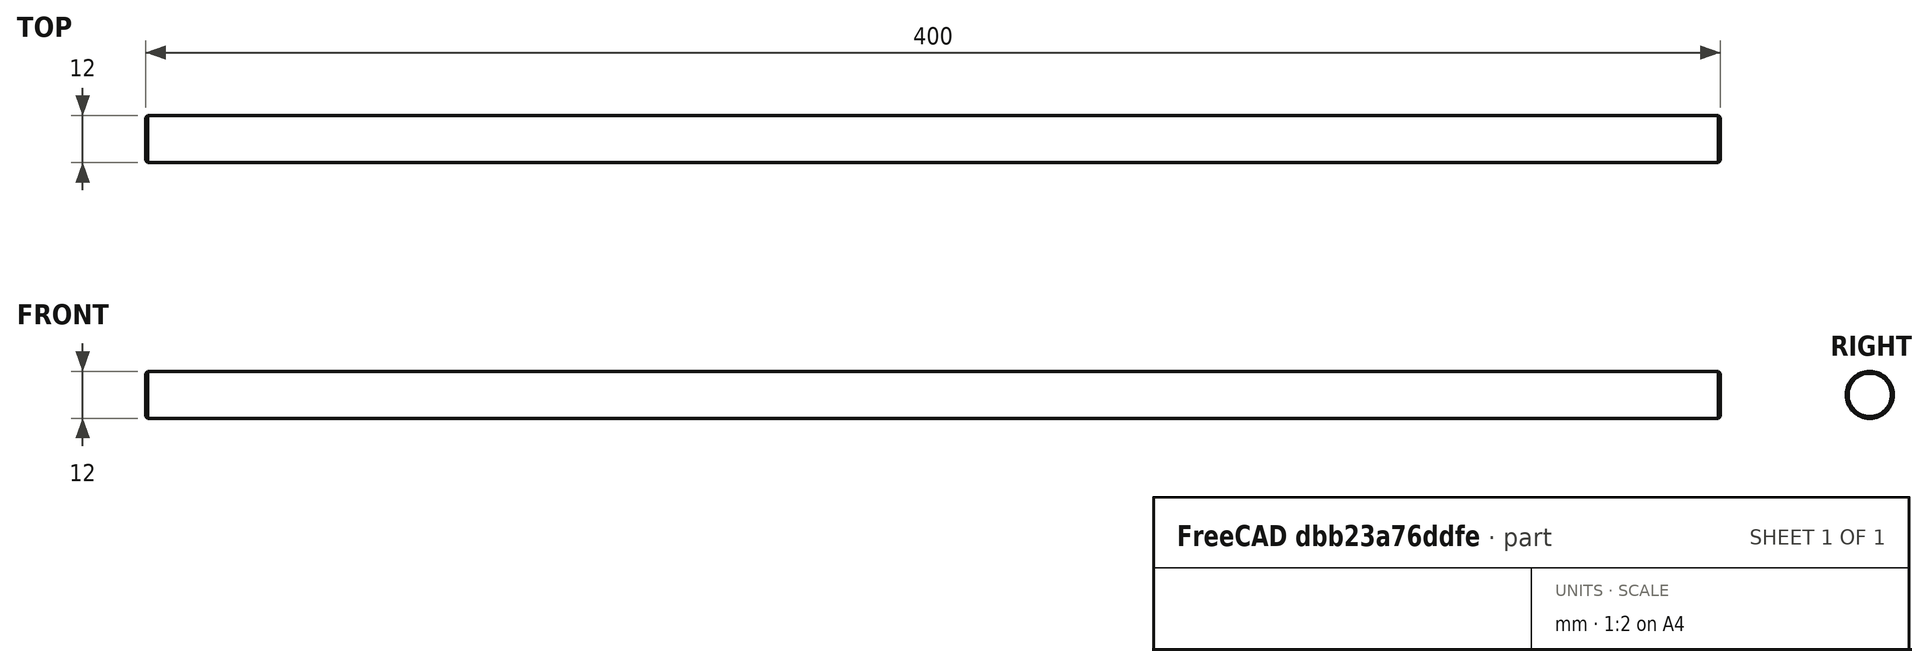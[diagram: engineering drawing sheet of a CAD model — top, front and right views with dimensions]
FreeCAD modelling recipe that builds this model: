
FCSTD DOCUMENT  (FreeCAD 0.15R4671 (Git))
Label: rod-400
License: All rights reserved
LicenseURL: http://en.wikipedia.org/wiki/All_rights_reserved
objects: Sketcher::SketchObject×1, PartDesign::Pad×1, PartDesign::Chamfer×1
note: 4 computed .brp shape members not serialized (recipe doc carries the construction recipe); baked Part::Feature solids carry a one-line shape summary decoded from their .brp

FEATURE [Sketcher::SketchObject] Sketch  label="rod-sketch"
  Placement = pos=(0,0,0) rot=(0.57735,0.57735,0.57735;2.0944rad)
  sketch-geometry (1):
    g0: Circle CenterX=0 CenterY=0 CenterZ=0 NormalX=0 NormalY=0 NormalZ=1 Radius=6
  constraints (2):
    c: Coincident(g0,g-1)
    c: Radius(g0) = 6
FEATURE [PartDesign::Pad] Pad  label="rod"
  Length = 400
  Length2 = 100
  Midplane = true
  Placement = pos=(0,0,0) rot=(0.57735,0.57735,0.57735;2.0944rad)
  Sketch = -> Sketch
  Type = 0
FEATURE [PartDesign::Chamfer] Chamfer  label="rod-400"
  Base = -> Pad [Edge3,Edge2]
  Placement = pos=(0,0,0) rot=(0.57735,0.57735,0.57735;2.0944rad)
  Size = 0.5
